# Revit family: 3080025 Feilo Sylvania Lighting Fixtures INVERTO DIRECT NW EB BLACK
name_source: partatom
category: Lighting Fixtures
revit_build: Autodesk Revit 2017 (Build: 20190507_1515(x64)
units: mm (PartAtom-declared; Revit-internal decimal feet)

## family parameters
Cut with Voids When Loaded = No
Host = Face
Light Source = Yes
Part Type = Normal
Room Calculation Point = No
Round Connector Dimension = Use Diameter
Shared = No

## types (1)
- 3080025 INVERTO DIRECT NW EB BLACK
    Apparent Load = 16 VA
    Assembly Code = D5020200
    AssetType = Fixed
    Calculate Coefficient of Utilization = No
    Color Filter = 16777215
    Cost = 0 $
    Default Elevation = 1219 mm
    Description = Surface Wall mounted luminaire, wire to base with pluggable connection for easy installation,  suitable for looping, switchable driver, black coloured aluminium housing, 1,617lm or 2,045lm, 16W or 19W, 102lm/W or 107lm/W, 4000K, 350mA or 450mA , CRI:80,  40° beam Angle, non-dimmable, IP65, IK02, 50,000hrs (L70),  23.00x19.4x11.5mm.
    Dimming Lamp Color Temperature Shift = <None>
    DimmingControlOptions = Non dimmable
    DocumentationLiterature = http://www.sylvania-lighting.com
    DurationUnit = hours
    ElectricShockClassification = Class I
    Emit Shape Visible in Rendering = No
    Emit from Rectangle Length = 90 mm  [stored 0.295276 ft]
    Emit from Rectangle Width = 90 mm  [stored 0.295276 ft]
    ExpectedLife = 50000
    Housing material = Default
    IfcExportAs = IfcLightFixtureType
    IfcExportType = IfcLightFixtureType
    ImpactProtectionIndex = IK07
    IngressProtection = IP65
    InputNominalFrequency = 50/60 Hz
    InputVoltage = 220-240V~
    Keynote = 16500
    Lamp = LED
    LampColourRenderingIndex = 80
    LampColourTemperature = 4000 K
    LampNominalLuminous = 1617 / 2045 lm
    LampsType = LED
    LightOutputRatio = 100
    LuminousEfficacy = 102 lm/W
    Manufacturer = Feilo Sylvania
    ManufacturerName = Feilo Sylvania
    Material = aluminium housing, glass diffuser
    Model = INVERTO DIRECT NW EB BLACK
    ModelNumber = 3080025
    ModelReference = INVERTO DIRECT NW EB BLACK
    Name = INVERTO DIRECT NW EB BLACK
    NominalDepth = 110 mm  [stored 0.360892 ft]
    NominalHeight = 110 mm  [stored 0.360892 ft]
    NominalLength = 162 mm
    Photometric Web File = 3080025.ies
    PowerConsumption = 16 W
    PowerFactor = 0
    Tilt Angle = -90.00°
    Type Image = <None>
    TypeName = INVERTO DIRECT NW EB BLACK
    URL = http://www.sylvania-lighting.com
    Voltage = 230 V
    Weight = 1.461 kg

note: [stored X ft] marks values corroborated as IEEE doubles in the binary element streams (Revit-internal decimal feet)

## geometry (parser evidence)
native form markers: Sweep x2
no freeform markers — native parametric forms only
